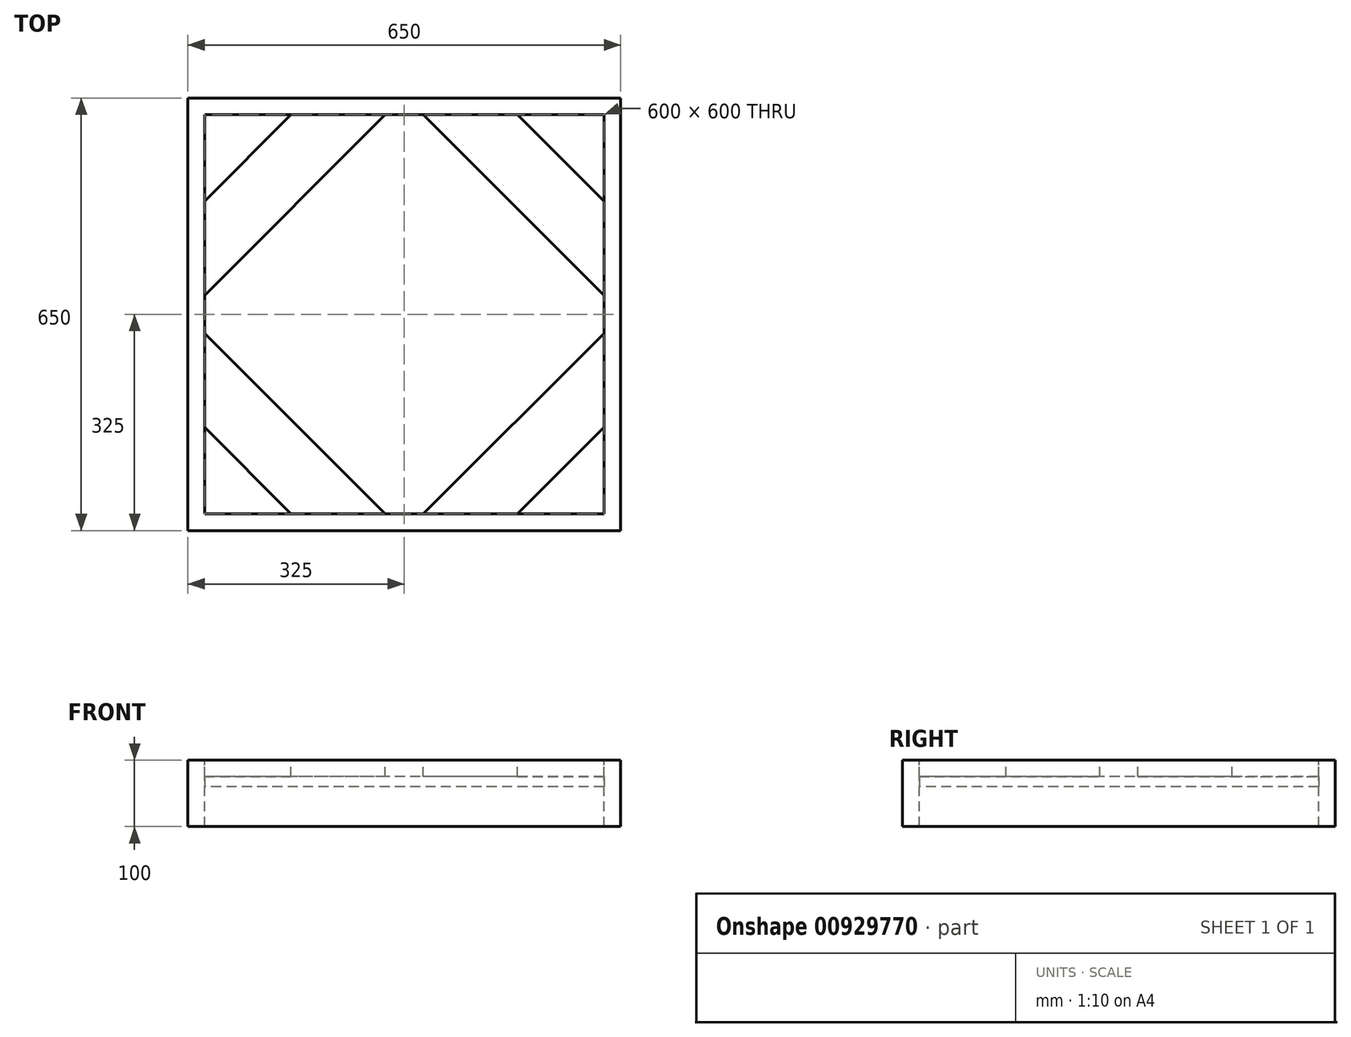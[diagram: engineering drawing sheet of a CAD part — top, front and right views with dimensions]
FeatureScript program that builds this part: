
annotation { "Feature Type Name" : "Feature", "Feature Type Description" : "" }
export const myFeature = defineFeature(function(context is Context, id is Id, definition is map)
    precondition{}
    {
        {
            var Q0;
            Q0=qCreatedBy(makeId("Top.planeOp"),FACE);
            var sketch = newSketch(context, id + "F0", { "sketchPlane" : qUnion([Q0])});
            skLineSegment(sketch, "E0.bottom", {"start": v(300, 300) * mm, "end": v(-300, 300) * mm});
            skLineSegment(sketch, "E0.top", {"start": v(300, -300) * mm, "end": v(-300, -300) * mm});
            skLineSegment(sketch, "E0.left", {"start": v(300, 300) * mm, "end": v(300, -300) * mm});
            skLineSegment(sketch, "E0.right", {"start": v(-300, 300) * mm, "end": v(-300, -300) * mm});
            skPoint(sketch, "E0.middle", {"position": v(0, 0) * mm});
            skSolve(sketch);
        }
        {
            var Q0;
            Q0 = qSketchRegion(id + "F0", true);
            extrude(context, id + "F1", {"entities" : qUnion([Q0]), "depth" : 15 * mm, "offsetDistance" : 25 * mm});
        }
        {
            var Q0;
            Q0=makeQuery(id+"F1.opExtrude","CAP_FACE",FACE,{"disambiguationData":[OSD([sQuery(id+"F0.wireOp",EDGE,"E0.bottom"),sQuery(id+"F0.wireOp",EDGE,"E0.top"),sQuery(id+"F0.wireOp",EDGE,"E0.left"),sQuery(id+"F0.wireOp",EDGE,"E0.right")])],"isStart":false});
            var sketch = newSketch(context, id + "F2", { "sketchPlane" : qUnion([Q0])});
            skLineSegment(sketch, "E1", {"start": v(-300, 300) * mm, "end": v(-300, -300) * mm});
            skLineSegment(sketch, "E2", {"start": v(-300, -300) * mm, "end": v(-210, -210) * mm});
            skLineSegment(sketch, "E3", {"start": v(-210, -210) * mm, "end": v(-210, 210) * mm});
            skLineSegment(sketch, "E4", {"start": v(-210, 210) * mm, "end": v(-300, 300) * mm});
            skLineSegment(sketch, "E5", {"start": v(300, 300) * mm, "end": v(210, 210) * mm});
            skLineSegment(sketch, "E6", {"start": v(210, 210) * mm, "end": v(210, -210) * mm});
            skLineSegment(sketch, "E7", {"start": v(210, -210) * mm, "end": v(300, -300) * mm});
            skLineSegment(sketch, "E8", {"start": v(300, -300) * mm, "end": v(300, 300) * mm});
            skLineSegment(sketch, "E9", {"start": v(-210, 210) * mm, "end": v(210, 210) * mm});
            skLineSegment(sketch, "E10", {"start": v(210, 210) * mm, "end": v(300, 300) * mm});
            skLineSegment(sketch, "E11", {"start": v(300, 300) * mm, "end": v(-300, 300) * mm});
            skLineSegment(sketch, "E12", {"start": v(-300, 300) * mm, "end": v(-210, 210) * mm});
            skLineSegment(sketch, "E13", {"start": v(-210, -210) * mm, "end": v(210, -210) * mm});
            skLineSegment(sketch, "E14", {"start": v(300, -300) * mm, "end": v(-300, -300) * mm});
            skSolve(sketch);
        }
        {
            var Q0;
            Q0=makeQuery(id+"F2.imprint","IMPRINT",FACE,{"disambiguationData":[TD([[makeQuery(id+"F2.imprint","IMPRINT",EDGE,{"derivedFrom":sQuery(id+"F2.wireOp",EDGE,"E3")}),-1.0]])]});
            var sketch = newSketch(context, id + "F3", { "sketchPlane" : qUnion([Q0])});
            skLineSegment(sketch, "E15.bottom", {"start": v(325, 325) * mm, "end": v(-325, 325) * mm});
            skLineSegment(sketch, "E15.top", {"start": v(325, -325) * mm, "end": v(-325, -325) * mm});
            skLineSegment(sketch, "E15.left", {"start": v(325, 325) * mm, "end": v(325, -325) * mm});
            skLineSegment(sketch, "E15.right", {"start": v(-325, 325) * mm, "end": v(-325, -325) * mm});
            skPoint(sketch, "E15.middle", {"position": v(0, 0) * mm});
            skLineSegment(sketch, "E16.bottom", {"start": v(300, 300) * mm, "end": v(-300, 300) * mm});
            skLineSegment(sketch, "E16.top", {"start": v(300, -300) * mm, "end": v(-300, -300) * mm});
            skLineSegment(sketch, "E16.left", {"start": v(300, 300) * mm, "end": v(300, -300) * mm});
            skLineSegment(sketch, "E16.right", {"start": v(-300, 300) * mm, "end": v(-300, -300) * mm});
            skSolve(sketch);
        }
        {
            var Q0;
            Q0=makeQuery(id+"F3.imprint","IMPRINT",FACE,{"disambiguationData":[TD([[makeQuery(id+"F3.imprint","IMPRINT",EDGE,{"derivedFrom":sQuery(id+"F3.wireOp",EDGE,"E15.bottom")}),1.0]])]});
            extrude(context, id + "F4", {"entities" : qUnion([Q0]), "oppositeDirection" : true, "depth" : 75 * mm, "offsetDistance" : 25 * mm, "hasSecondDirection" : true, "secondDirectionOppositeDirection" : false, "secondDirectionDepth" : 25 * mm});
        }
        {
            var Q0;
            Q0=makeQuery(id+"F4.opExtrude","CAP_FACE",FACE,{"disambiguationData":[OSD([sQuery(id+"F3.wireOp",EDGE,"E15.bottom"),sQuery(id+"F3.wireOp",EDGE,"E15.top"),sQuery(id+"F3.wireOp",EDGE,"E15.left"),sQuery(id+"F3.wireOp",EDGE,"E15.right"),sQuery(id+"F3.wireOp",EDGE,"E16.bottom"),sQuery(id+"F3.wireOp",EDGE,"E16.top"),sQuery(id+"F3.wireOp",EDGE,"E16.left"),sQuery(id+"F3.wireOp",EDGE,"E16.right")])],"isStart":true});
            var sketch = newSketch(context, id + "F5", { "sketchPlane" : qUnion([Q0])});
            skLineSegment(sketch, "E17", {"start": v(-170, 300) * mm, "end": v(-300, 170) * mm});
            skLineSegment(sketch, "E18", {"start": v(-300, 170) * mm, "end": v(-300, 28.58) * mm});
            skLineSegment(sketch, "E19", {"start": v(-300, 28.58) * mm, "end": v(-28.58, 300) * mm});
            skLineSegment(sketch, "E20", {"start": v(-28.58, 300) * mm, "end": v(-170, 300) * mm});
            skLineSegment(sketch, "E21", {"start": v(170, 300) * mm, "end": v(300, 170) * mm});
            skLineSegment(sketch, "E22", {"start": v(300, 170) * mm, "end": v(300, 28.58) * mm});
            skLineSegment(sketch, "E23", {"start": v(300, 28.58) * mm, "end": v(28.58, 300) * mm});
            skLineSegment(sketch, "E24", {"start": v(28.58, 300) * mm, "end": v(170, 300) * mm});
            skLineSegment(sketch, "E25", {"start": v(300, -170) * mm, "end": v(170, -300) * mm});
            skLineSegment(sketch, "E26", {"start": v(170, -300) * mm, "end": v(28.58, -300) * mm});
            skLineSegment(sketch, "E27", {"start": v(28.58, -300) * mm, "end": v(300, -28.58) * mm});
            skLineSegment(sketch, "E28", {"start": v(300, -28.58) * mm, "end": v(300, -170) * mm});
            skLineSegment(sketch, "E29", {"start": v(-28.58, -300) * mm, "end": v(-300, -28.58) * mm});
            skLineSegment(sketch, "E30", {"start": v(-300, -28.58) * mm, "end": v(-300, -170) * mm});
            skLineSegment(sketch, "E31", {"start": v(-300, -170) * mm, "end": v(-170, -300) * mm});
            skSolve(sketch);
        }
        {
            var Q0;
            Q0 = qSketchRegion(id + "F5", true);
            var Q1;
            {var subQ0=sQuery(id+"F5.wireOp",EDGE,"E29");Q1=makeQuery(id+"F5.imprint","IMPRINT",FACE,{"disambiguationData":[TD([[makeQuery(id+"F5.imprint","IMPRINT",EDGE,{"derivedFrom":subQ0}),1.0]])]});}
            extrude(context, id + "F6", {"entities" : qUnion([Q0, Q1]), "oppositeDirection" : true, "depth" : 25 * mm, "offsetDistance" : 25 * mm});
        }
    });
